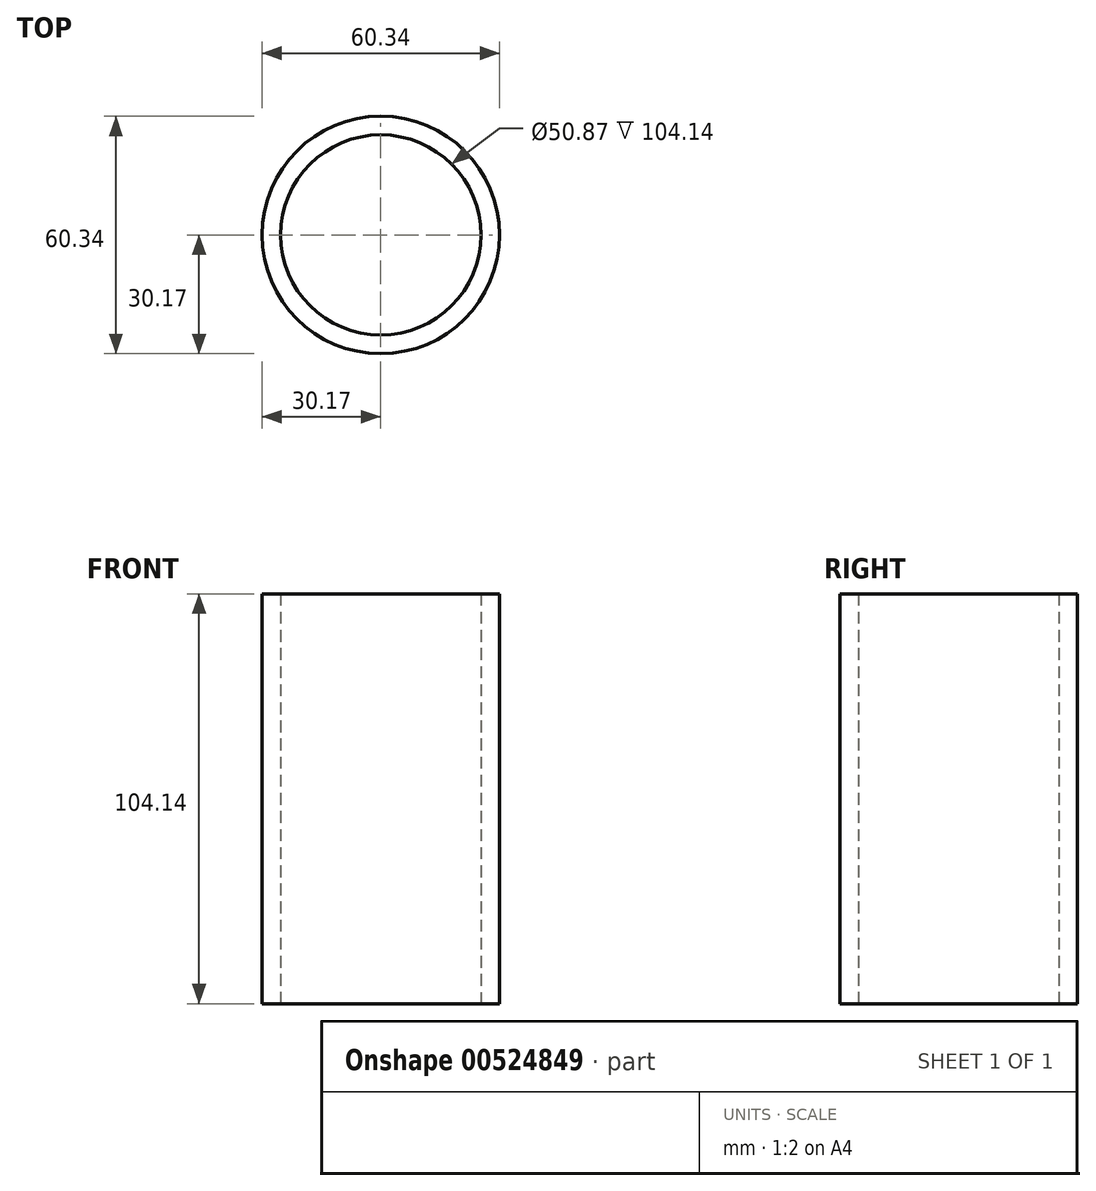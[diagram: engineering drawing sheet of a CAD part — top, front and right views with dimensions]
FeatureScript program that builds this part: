
annotation { "Feature Type Name" : "Feature", "Feature Type Description" : "" }
export const myFeature = defineFeature(function(context is Context, id is Id, definition is map)
    precondition{}
    {
        {
            var Q0;
            Q0=qCreatedBy(makeId("Top.planeOp"),FACE);
            var sketch = newSketch(context, id + "F0", { "sketchPlane" : qUnion([Q0])});
            skCircle(sketch, "E0", {"center": v(0, 0) * mm, "radius": 30.17 * mm});
            skCircle(sketch, "E1", {"center": v(0, 0) * mm, "radius": 25.44 * mm});
            skSolve(sketch);
        }
        {
            var Q0;
            Q0 = qSketchRegion(id + "F0", true);
            extrude(context, id + "F1", {"entities" : qUnion([Q0]), "depth" : 104.14 * mm, "offsetDistance" : 25.4 * mm});
        }
    });
